# Revit family: Magnuson-Boden-Bench+
name_source: partatom
category: Furniture
units: mm (PartAtom-declared; Revit-internal decimal feet)

## family parameters
Always vertical = Yes
Cut with Voids When Loaded = No
Room Calculation Point = No
Shared = No
Work Plane-Based = No

## types (1)
- BOD-B-01
    Assembly Code = E2020200
    B-Mount Finish = MAG - Stainless Steel
    B-Skate Finish = MAG - Burnished Aluminum
    Default Elevation = 0"
    Depth = 17 3/4"
    Description = Outdoor High Performance Cast Concrete Bench
    Height = 16 1/2"
    Keynote = 12500
    Low Emitting Finish = Yes
    Low Emitting Material = Yes
    Manufacturer = Magnuson Group
    Model = BOD-B-01
    Percentage of Recycled Content = 0
    Revit Model Built By = https://servex-us.com
    Salvage or Reuse = Yes
    Seat Finish = MAG - Concrete
    Type Comments = Boden
    URL = www.magnusongroup.com
    Width = 61 1/2"

## geometry (parser evidence)
native form markers: Sweep x8
no freeform markers — native parametric forms only
